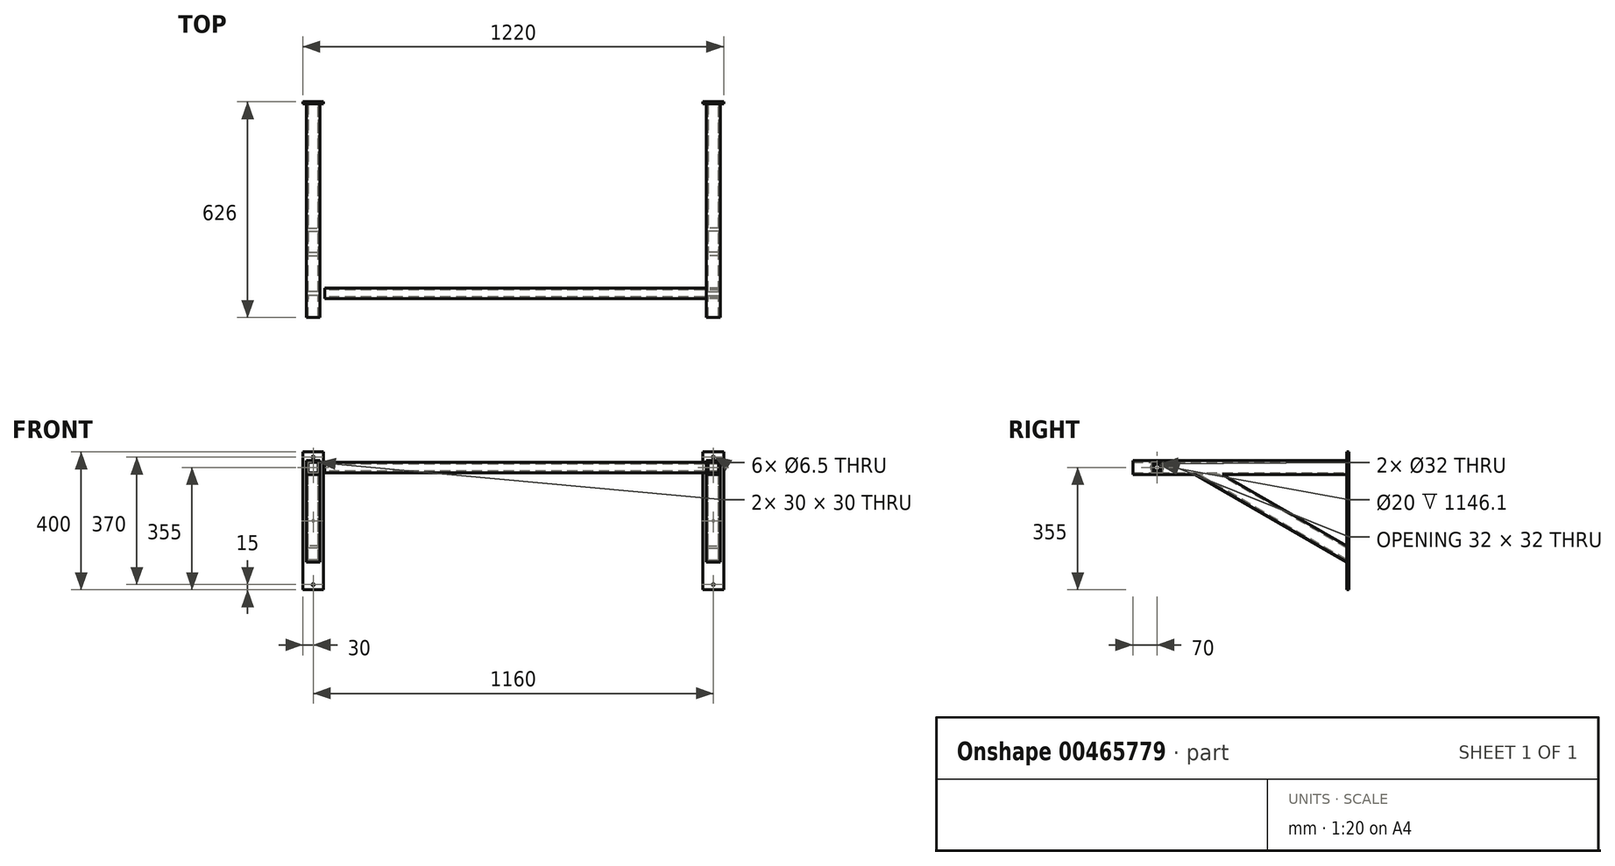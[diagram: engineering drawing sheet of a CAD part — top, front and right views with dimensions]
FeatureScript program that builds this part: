
annotation { "Feature Type Name" : "Feature", "Feature Type Description" : "" }
export const myFeature = defineFeature(function(context is Context, id is Id, definition is map)
    precondition{}
    {
        {
            var Q0;
            Q0=qCreatedBy(makeId("Right.planeOp"),FACE);
            var sketch = newSketch(context, id + "F0", { "sketchPlane" : qUnion([Q0])});
            skCircle(sketch, "E0", {"center": v(0, 0) * mm, "radius": 15 * mm});
            skCircle(sketch, "E1", {"center": v(0, 0) * mm, "radius": 10 * mm});
            skSolve(sketch);
        }
        {
            var Q0;
            Q0=makeQuery(id+"F0.imprint","IMPRINT",FACE,{"disambiguationData":[TD([[makeQuery(id+"F0.imprint","IMPRINT",EDGE,{"derivedFrom":sQuery(id+"F0.wireOp",EDGE,"E0")}),1.0]])]});
            extrude(context, id + "F1", {"entities" : qUnion([Q0]), "depth" : 600 * mm, "hasSecondDirection" : true, "secondDirectionOppositeDirection" : true, "secondDirectionDepth" : 600 * mm});
        }
        {
            var Q0;
            Q0=qCreatedBy(makeId("Front.planeOp"),FACE);
            cPlane(context, id + "F2", {"entities" : qUnion([Q0]), "cplaneType" : CPlaneType.OFFSET, "offset" : 550 * mm, "oppositeDirection" : true, "width" : 150 * mm, "height" : 150 * mm});
        }
        {
            var Q0;
            Q0=qCreatedBy(id+"F2.planeOp",FACE);
            var sketch = newSketch(context, id + "F3", { "sketchPlane" : qUnion([Q0])});
            skLineSegment(sketch, "E2.bottom", {"start": v(-600, 20) * mm, "end": v(-560, 20) * mm});
            skLineSegment(sketch, "E2.top", {"start": v(-600, -20) * mm, "end": v(-560, -20) * mm});
            skLineSegment(sketch, "E2.left", {"start": v(-600, 20) * mm, "end": v(-600, -20) * mm});
            skLineSegment(sketch, "E2.right", {"start": v(-560, 20) * mm, "end": v(-560, -20) * mm});
            skLineSegment(sketch, "E3", {"start": v(-600.87, 0) * mm, "end": v(-458.2, 0) * mm, "construction": true});
            skLineSegment(sketch, "E4.0", {"start": v(-595, 15) * mm, "end": v(-565, 15) * mm});
            skLineSegment(sketch, "E4.1", {"start": v(-595, 15) * mm, "end": v(-595, -15) * mm});
            skLineSegment(sketch, "E4.2", {"start": v(-595, -15) * mm, "end": v(-565, -15) * mm});
            skLineSegment(sketch, "E4.3", {"start": v(-565, 15) * mm, "end": v(-565, -15) * mm});
            skSolve(sketch);
        }
        {
            var Q0;
            Q0=makeQuery(id+"F3.imprint","IMPRINT",FACE,{"disambiguationData":[TD([[makeQuery(id+"F3.imprint","IMPRINT",EDGE,{"derivedFrom":sQuery(id+"F3.wireOp",EDGE,"E2.bottom")}),-1.0]])]});
            extrude(context, id + "F4", {"entities" : qUnion([Q0]), "depth" : 620 * mm});
        }
        {
            var Q0;
            Q0=makeQuery(id+"F4.opExtrude","SWEPT_FACE",FACE,{"disambiguationData":[OSD([sQuery(id+"F3.wireOp",EDGE,"E2.left")])]});
            var sketch = newSketch(context, id + "F5", { "sketchPlane" : qUnion([Q0])});
            skCircle(sketch, "E5.0", {"center": v(0, 0) * mm, "radius": 15 * mm, "construction": true});
            skCircle(sketch, "E6", {"center": v(0, 0) * mm, "radius": 16 * mm});
            skSolve(sketch);
        }
        {
            var Q0;
            Q0=makeQuery(id+"F5.imprint","IMPRINT",FACE,{"disambiguationData":[TD([[makeQuery(id+"F5.imprint","IMPRINT",EDGE,{"derivedFrom":sQuery(id+"F5.wireOp",EDGE,"E6")}),1.0]])]});
            var Q1;
            Q1=sQuery(id+"F5.wireOp",EDGE,"E5.0");
            extrude(context, id + "F6", {"entities" : qUnion([Q0]), "operationType" : NewBodyOperationType.REMOVE, "surfaceEntities" : qUnion([Q1]), "oppositeDirection" : true, "depth" : 53.9 * mm});
        }
        {
            var Q0;
            Q0=qCreatedBy(id+"F2.planeOp",FACE);
            var sketch = newSketch(context, id + "F7", { "sketchPlane" : qUnion([Q0])});
            skLineSegment(sketch, "E7.bottom", {"start": v(-550, 45) * mm, "end": v(-610, 45) * mm});
            skLineSegment(sketch, "E7.top", {"start": v(-550, -355) * mm, "end": v(-610, -355) * mm});
            skLineSegment(sketch, "E7.left", {"start": v(-550, 45) * mm, "end": v(-550, -355) * mm});
            skLineSegment(sketch, "E7.right", {"start": v(-610, 45) * mm, "end": v(-610, -355) * mm});
            skLineSegment(sketch, "E8", {"start": v(-580, 46.66) * mm, "end": v(-580, -42.74) * mm, "construction": true});
            skCircle(sketch, "E9", {"center": v(-580, 30) * mm, "radius": 3.25 * mm});
            skLineSegment(sketch, "E10", {"start": v(-550, -155) * mm, "end": v(-610, -155) * mm, "construction": true});
            skCircle(sketch, "E11.MirrorC", {"center": v(-580, -340) * mm, "radius": 3.25 * mm});
            skCircle(sketch, "E12", {"center": v(-580, -155) * mm, "radius": 3.25 * mm});
            skSolve(sketch);
        }
        {
            var Q0;
            Q0=makeQuery(id+"F7.imprint","IMPRINT",FACE,{"disambiguationData":[TD([[makeQuery(id+"F7.imprint","IMPRINT",EDGE,{"derivedFrom":sQuery(id+"F7.wireOp",EDGE,"E7.bottom")}),1.0]])]});
            extrude(context, id + "F8", {"entities" : qUnion([Q0]), "oppositeDirection" : true, "depth" : 6 * mm, "offsetDistance" : 25 * mm});
        }
        {
            var Q0;
            Q0=makeQuery(id+"F4.opExtrude","CAP_EDGE",EDGE,{"disambiguationData":[OSD([sQuery(id+"F3.wireOp",EDGE,"E2.top")])],"isStart":true});
            cPlane(context, id + "F9", {"entities" : qUnion([Q0]), "cplaneType" : CPlaneType.LINE_ANGLE, "offset" : 25 * mm, "angle" : 30 * degree, "oppositeDirection" : true, "width" : 150 * mm, "height" : 150 * mm});
        }
        {
            var Q0;
            Q0=qCreatedBy(id+"F9.planeOp",FACE);
            var sketch = newSketch(context, id + "F10", { "sketchPlane" : qUnion([Q0])});
            skLineSegment(sketch, "E13.bottom", {"start": v(600, 77.68) * mm, "end": v(560, 77.68) * mm});
            skLineSegment(sketch, "E13.top", {"start": v(600, 37.68) * mm, "end": v(560, 37.68) * mm});
            skLineSegment(sketch, "E13.left", {"start": v(600, 77.68) * mm, "end": v(600, 37.68) * mm});
            skLineSegment(sketch, "E13.right", {"start": v(560, 77.68) * mm, "end": v(560, 37.68) * mm});
            skLineSegment(sketch, "E14.0", {"start": v(595, 72.68) * mm, "end": v(565, 72.68) * mm});
            skLineSegment(sketch, "E14.1", {"start": v(595, 72.68) * mm, "end": v(595, 42.68) * mm});
            skLineSegment(sketch, "E14.2", {"start": v(595, 42.68) * mm, "end": v(565, 42.68) * mm});
            skLineSegment(sketch, "E14.3", {"start": v(565, 72.68) * mm, "end": v(565, 42.68) * mm});
            skLineSegment(sketch, "E15", {"start": v(580, 232.9) * mm, "end": v(580, 70.22) * mm, "construction": true});
            skSolve(sketch);
        }
        {
            var Q0;
            Q0=makeQuery(id+"F10.imprint","IMPRINT",FACE,{"disambiguationData":[TD([[makeQuery(id+"F10.imprint","IMPRINT",EDGE,{"derivedFrom":sQuery(id+"F10.wireOp",EDGE,"E13.bottom")}),1.0]])]});
            var Q1;
            {var subQ0=sQuery(id+"F7.wireOp",EDGE,"E11.MirrorC");var subQ1=sQuery(id+"F7.wireOp",EDGE,"E9");var subQ2=sQuery(id+"F7.wireOp",EDGE,"E7.right");var subQ3=sQuery(id+"F7.wireOp",EDGE,"E7.bottom");var subQ4=sQuery(id+"F7.wireOp",EDGE,"E7.left");var subQ5=sQuery(id+"F7.wireOp",EDGE,"E7.top");var subQ6=sQuery(id+"F7.wireOp",EDGE,"E12");Q1=makeQuery(id+"F8.boolean.opBoolean","SPLIT",FACE,{"disambiguationData":[TD([makeQuery(id+"F4.opExtrude","SWEPT_FACE",FACE,{"disambiguationData":[OSD([sQuery(id+"F3.wireOp",EDGE,"E2.bottom")])]})])],"derivedFrom":makeQuery(id+"F8.opExtrude","CAP_FACE",FACE,{"disambiguationData":[OSD([subQ3,subQ5,subQ4,subQ2,subQ1,subQ0,subQ6])],"isStart":true})});}
            extrude(context, id + "F11", {"entities" : qUnion([Q0]), "endBound" : BoundingType.UP_TO_SURFACE, "endBoundEntityFace" : qUnion([Q1]), "depth" : 25 * mm});
        }
        {
            var Q0;
            Q0=makeQuery(id+"F11.opExtrude","CAP_FACE",FACE,{"disambiguationData":[OSD([sQuery(id+"F10.wireOp",EDGE,"E13.bottom"),sQuery(id+"F10.wireOp",EDGE,"E13.top"),sQuery(id+"F10.wireOp",EDGE,"E13.left"),sQuery(id+"F10.wireOp",EDGE,"E13.right"),sQuery(id+"F10.wireOp",EDGE,"E14.0"),sQuery(id+"F10.wireOp",EDGE,"E14.1"),sQuery(id+"F10.wireOp",EDGE,"E14.2"),sQuery(id+"F10.wireOp",EDGE,"E14.3")])],"isStart":true});
            var Q1;
            Q1=makeQuery(id+"F4.opExtrude","SWEPT_FACE",FACE,{"disambiguationData":[OSD([sQuery(id+"F3.wireOp",EDGE,"E2.top")])]});
            extrude(context, id + "F12", {"entities" : qUnion([Q0]), "operationType" : NewBodyOperationType.ADD, "endBound" : BoundingType.UP_TO_SURFACE, "endBoundEntityFace" : qUnion([Q1]), "depth" : 25 * mm});
        }
        {
            var Q0;
            Q0=makeQuery(id+"F4.opExtrude","SWEPT_BODY",BODY,{"disambiguationData":[OSD([sQuery(id+"F3.wireOp",EDGE,"E2.bottom"),sQuery(id+"F3.wireOp",EDGE,"E2.top"),sQuery(id+"F3.wireOp",EDGE,"E2.left"),sQuery(id+"F3.wireOp",EDGE,"E2.right"),sQuery(id+"F3.wireOp",EDGE,"E4.0"),sQuery(id+"F3.wireOp",EDGE,"E4.1"),sQuery(id+"F3.wireOp",EDGE,"E4.2"),sQuery(id+"F3.wireOp",EDGE,"E4.3")])]});
            var Q1;
            Q1=makeQuery(id+"F8.opExtrude","SWEPT_BODY",BODY,{"disambiguationData":[OSD([sQuery(id+"F7.wireOp",EDGE,"E7.bottom"),sQuery(id+"F7.wireOp",EDGE,"E7.top"),sQuery(id+"F7.wireOp",EDGE,"E7.left"),sQuery(id+"F7.wireOp",EDGE,"E7.right"),sQuery(id+"F7.wireOp",EDGE,"E9"),sQuery(id+"F7.wireOp",EDGE,"E11.MirrorC"),sQuery(id+"F7.wireOp",EDGE,"E12")])]});
            var Q2;
            Q2=makeQuery(id+"F11.opExtrude","SWEPT_BODY",BODY,{"disambiguationData":[OSD([sQuery(id+"F10.wireOp",EDGE,"E13.bottom"),sQuery(id+"F10.wireOp",EDGE,"E13.top"),sQuery(id+"F10.wireOp",EDGE,"E13.left"),sQuery(id+"F10.wireOp",EDGE,"E13.right"),sQuery(id+"F10.wireOp",EDGE,"E14.0"),sQuery(id+"F10.wireOp",EDGE,"E14.1"),sQuery(id+"F10.wireOp",EDGE,"E14.2"),sQuery(id+"F10.wireOp",EDGE,"E14.3")])]});
            var Q3;
            Q3=qCreatedBy(makeId("Right.planeOp"),FACE);
            mirror(context, id + "F13", {"operationType" : NewBodyOperationType.ADD, "entities" : qUnion([Q0, Q1, Q2]), "mirrorPlane" : qUnion([Q3])});
        }
    });
